# Revit family: Genie_Site_ArticulatingBoom_(ZX-135-70)1
name_source: partatom
category: Site
revit_build: Autodesk Revit 2017 (Build: 20160225_1515(x64)
units: mm (PartAtom-declared; Revit-internal decimal feet)

## family parameters
Always vertical = Yes
Cut with Voids When Loaded = No
OmniClass Number = 23.50.85.17.11
OmniClass Title = Electric and Battery Telescoping Platforms
Part Type = Normal
Round Connector Dimension = Use Diameter
Shared = No
Work Plane-Based = No

## types (1)
- ZX-135 / 70
    Assembly Code = E1030900
    AssetType = Fixed
    BIMObjectName = Genie_Site_ArticulatingBoom_(ZX-135-70)
    ClassificationName = Uniclass2015
    ClassificationValue = Pr_65_80_47_95
    Color = Grey & Blue
    Cost = 0 $
    Description = Ideal for outdoor construction and industrial applications, the Genie® ZX®-135/70 articulating boom lift delivers access to up, over and out applications inaccessible by a traditional jib. Four-wheel drive with full-time positive traction means that this articulating boom can handle rough jobsite ground conditions with ease.
    DocumentationLiterature = https://www.genielift.com
    DocumentationTechnical = https://www.genielift.com
    DurationUnit = Years
    ExpectedLife = 0
    Features = Mini Genie X-Chassis™ system extends and retracts to provide both stability on the job and a narrow profile for transport, Telescoping Jib-Extend™ jib extends from 12 to 20 ft (3.66 to 6.10 m) and provides a 110˚ vertical range of motion, 360˚ continuous rotation turntable and 160˚platform rotation for fast, easy positioning, Four-wheel steer with front-wheel, rear-wheel, crab and coordinated steer options available to provide additional maneuverability
    Finish = Painted Steel
    IfcExportAs = IfcTransportElement
    IfcExportType = IfcTransportElementType
    Keynote = X
    Manufacturer = Genie
    ManufacturerName = Genie
    Material = Painted Steel
    Model = Genie - Articulating Boom
    ModelNumber = ZX-135 / 70
    ModelReference = Genie - Articulating Boom
    NBSDescription = Vertical lifting platforms
    NBSObjectName = Genie - Vertical lifting platforms
    NBSReference = 90-80-65/350
    NominalDepth = 2490 mm
    NominalHeight = 3090 mm
    NominalLength = 12930 mm
    ProductionYear = 2018
    ReplacementCost = 0
    Size = 3.49m x 3.09m x 12.93m
    Type Comments = ZX-135 / 70
    TypeName = Genie - Articulating Boom
    URL = http://www.genielift.co.uk
    WarrantyDurationLabor = 0
    WarrantyDurationParts = 0
    WarrantyDurationUnit = Years
    WarrantyGuarantorLabor = http://www.genielift.co.uk
    WarrantyGuarantorParts = http://www.genielift.co.uk
    _BSBibleVersion = 15
    _BimSpecGuid = 0
    _CurrentRevision = 1
    _DistributedBy = www.bimstore.co.uk

## geometry (parser evidence)
native form markers: Sweep x54
no freeform markers — native parametric forms only
